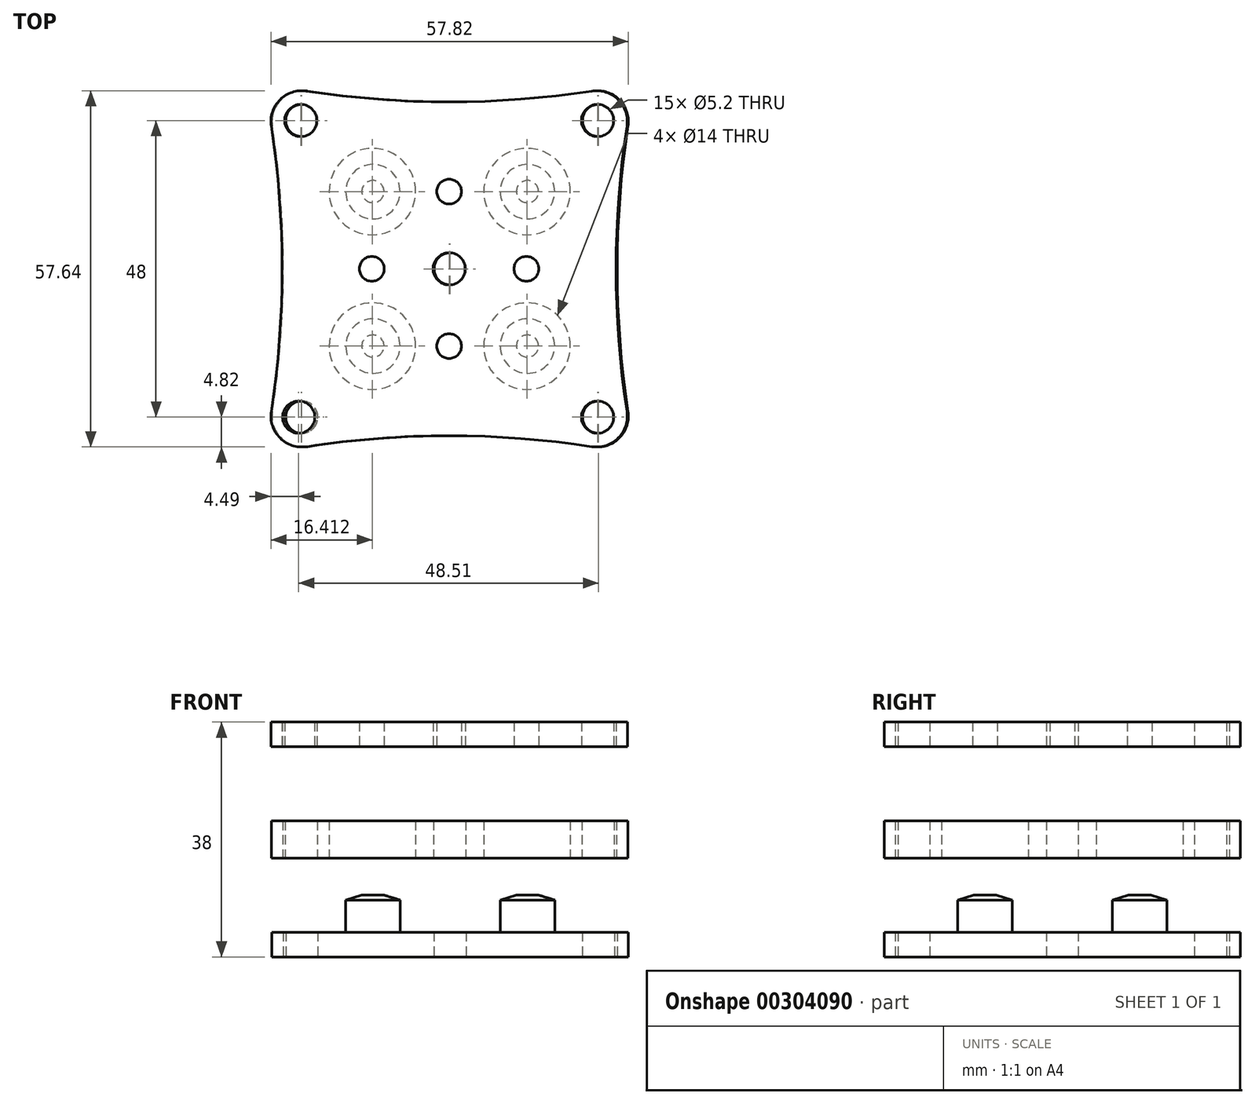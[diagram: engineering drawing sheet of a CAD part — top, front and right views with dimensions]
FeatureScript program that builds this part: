
annotation { "Feature Type Name" : "Feature", "Feature Type Description" : "" }
export const myFeature = defineFeature(function(context is Context, id is Id, definition is map)
    precondition{}
    {
        {
            var Q0;
            Q0=qCreatedBy(makeId("Top.planeOp"),FACE);
            var sketch = newSketch(context, id + "F0", { "sketchPlane" : qUnion([Q0])});
            skLineSegment(sketch, "E0.bottom", {"start": v(12.5, -12.5) * mm, "end": v(-12.5, -12.5) * mm});
            skLineSegment(sketch, "E0.top", {"start": v(12.5, 12.5) * mm, "end": v(-12.5, 12.5) * mm});
            skLineSegment(sketch, "E0.left", {"start": v(12.5, -12.5) * mm, "end": v(12.5, 12.5) * mm});
            skLineSegment(sketch, "E0.right", {"start": v(-12.5, -12.5) * mm, "end": v(-12.5, 12.5) * mm});
            skPoint(sketch, "E0.middle", {"position": v(0, 0) * mm});
            skCircle(sketch, "E1", {"center": v(-12.5, 12.5) * mm, "radius": 7 * mm});
            skCircle(sketch, "E2", {"center": v(12.5, 12.5) * mm, "radius": 7 * mm});
            skCircle(sketch, "E3", {"center": v(-12.5, -12.5) * mm, "radius": 7 * mm});
            skCircle(sketch, "E4", {"center": v(12.5, -12.5) * mm, "radius": 7 * mm});
            skCircle(sketch, "E5", {"center": v(-12.5, 12.5) * mm, "radius": 4.4 * mm});
            skCircle(sketch, "E6", {"center": v(12.5, 12.5) * mm, "radius": 4.4 * mm});
            skCircle(sketch, "E7", {"center": v(12.5, -12.5) * mm, "radius": 4.4 * mm});
            skCircle(sketch, "E8", {"center": v(-12.5, -12.5) * mm, "radius": 4.4 * mm});
            skCircle(sketch, "E9", {"center": v(0, 0) * mm, "radius": 2.6 * mm});
            skLineSegment(sketch, "E10.bottom", {"start": v(30, -30) * mm, "end": v(-30, -30) * mm});
            skLineSegment(sketch, "E10.top", {"start": v(30, 30) * mm, "end": v(-30, 30) * mm});
            skLineSegment(sketch, "E10.left", {"start": v(30, -30) * mm, "end": v(30, 30) * mm});
            skLineSegment(sketch, "E10.right", {"start": v(-30, -30) * mm, "end": v(-30, 30) * mm});
            skPoint(sketch, "E11.centerSnap0", {"position": v(0, -30) * mm});
            skCircle(sketch, "E12.cCircle", {"center": v(0, 0) * mm, "radius": 24 * mm, "construction": true});
            skLineSegment(sketch, "E12.0", {"start": v(24, 24) * mm, "end": v(24, -24) * mm});
            skLineSegment(sketch, "E12.1", {"start": v(24, -24) * mm, "end": v(-24, -24) * mm});
            skLineSegment(sketch, "E12.2", {"start": v(-24, -24) * mm, "end": v(-24, 24) * mm});
            skLineSegment(sketch, "E12.3", {"start": v(-24, 24) * mm, "end": v(24, 24) * mm});
            skPoint(sketch, "E12.0.midPoint", {"position": v(24, 0) * mm});
            skCircle(sketch, "E13", {"center": v(24, 24) * mm, "radius": 2.6 * mm});
            skCircle(sketch, "E14", {"center": v(-24, -24) * mm, "radius": 2.6 * mm});
            skCircle(sketch, "E15", {"center": v(24, -24) * mm, "radius": 2.6 * mm});
            skCircle(sketch, "E16", {"center": v(-24, 24) * mm, "radius": 2.6 * mm});
            skArc(sketch, "E17", {"start": v(-30, 30) * mm, "mid": v(0, 27) * mm, "end": v(30, 30) * mm});
            skArc(sketch, "E18", {"start": v(30, 30) * mm, "mid": v(27, 0) * mm, "end": v(30, -30) * mm});
            skArc(sketch, "E19", {"start": v(30, -30) * mm, "mid": v(0, -27) * mm, "end": v(-30, -30) * mm});
            skArc(sketch, "E20", {"start": v(-30, -30) * mm, "mid": v(-27, 0) * mm, "end": v(-30, 30) * mm});
            skSolve(sketch);
        }
        {
            var Q0;
            Q0=makeQuery(id+"F0.imprint","IMPRINT",FACE,{"disambiguationData":[TD([[makeQuery(id+"F0.imprint","IMPRINT",EDGE,{"derivedFrom":sQuery(id+"F0.wireOp",EDGE,"E17")}),-1.0]])]});
            var Q1;
            {var subQ5=sQuery(id+"F0.wireOp",EDGE,"E4");var subQ6=sQuery(id+"F0.wireOp",EDGE,"E0.bottom");var subQ7=makeQuery(id+"F0.imprint","INTERSECT",VERTEX,{"derivedFrom":[subQ6,subQ5]});Q1=makeQuery(id+"F0.imprint","IMPRINT",FACE,{"disambiguationData":[TD([[makeQuery(id+"F0.imprint","IMPRINT",EDGE,{"disambiguationData":[TD([[subQ7,-1.0]])],"derivedFrom":subQ6}),1.0]])]});}
            var Q2;
            {var subQ0=sQuery(id+"F0.wireOp",EDGE,"E6");var subQ1=sQuery(id+"F0.wireOp",EDGE,"E0.top");var subQ2=makeQuery(id+"F0.imprint","INTERSECT",VERTEX,{"derivedFrom":[subQ1,subQ0]});Q2=makeQuery(id+"F0.imprint","IMPRINT",FACE,{"disambiguationData":[TD([[makeQuery(id+"F0.imprint","IMPRINT",EDGE,{"disambiguationData":[TD([[subQ2,-1.0]])],"derivedFrom":subQ1}),-1.0]])]});}
            var Q3;
            {var subQ0=sQuery(id+"F0.wireOp",EDGE,"E7");var subQ1=sQuery(id+"F0.wireOp",EDGE,"E0.bottom");var subQ2=makeQuery(id+"F0.imprint","INTERSECT",VERTEX,{"derivedFrom":[subQ1,subQ0]});Q3=makeQuery(id+"F0.imprint","IMPRINT",FACE,{"disambiguationData":[TD([[makeQuery(id+"F0.imprint","IMPRINT",EDGE,{"disambiguationData":[TD([[subQ2,-1.0]])],"derivedFrom":subQ1}),1.0]])]});}
            var Q4;
            {var subQ0=sQuery(id+"F0.wireOp",EDGE,"E3");var subQ1=sQuery(id+"F0.wireOp",EDGE,"E0.bottom");var subQ2=makeQuery(id+"F0.imprint","INTERSECT",VERTEX,{"derivedFrom":[subQ1,subQ0]});Q4=makeQuery(id+"F0.imprint","IMPRINT",FACE,{"disambiguationData":[TD([[makeQuery(id+"F0.imprint","IMPRINT",EDGE,{"disambiguationData":[TD([[subQ2,-1.0]])],"derivedFrom":subQ1}),1.0]])]});}
            var Q5;
            {var subQ0=sQuery(id+"F0.wireOp",EDGE,"E1");var subQ1=sQuery(id+"F0.wireOp",EDGE,"E0.top");var subQ2=makeQuery(id+"F0.imprint","INTERSECT",VERTEX,{"derivedFrom":[subQ1,subQ0]});Q5=makeQuery(id+"F0.imprint","IMPRINT",FACE,{"disambiguationData":[TD([[makeQuery(id+"F0.imprint","IMPRINT",EDGE,{"disambiguationData":[TD([[subQ2,-1.0]])],"derivedFrom":subQ1}),-1.0]])]});}
            var Q6;
            Q6=makeQuery(id+"F0.imprint","IMPRINT",FACE,{"disambiguationData":[TD([[makeQuery(id+"F0.imprint","IMPRINT",EDGE,{"derivedFrom":sQuery(id+"F0.wireOp",EDGE,"E9")}),-1.0]])]});
            var Q7;
            {var subQ0=sQuery(id+"F0.wireOp",EDGE,"E7");var subQ1=sQuery(id+"F0.wireOp",EDGE,"E0.bottom");var subQ2=makeQuery(id+"F0.imprint","INTERSECT",VERTEX,{"derivedFrom":[subQ1,subQ0]});Q7=makeQuery(id+"F0.imprint","IMPRINT",FACE,{"disambiguationData":[TD([[makeQuery(id+"F0.imprint","IMPRINT",EDGE,{"disambiguationData":[TD([[subQ2,-1.0]])],"derivedFrom":subQ1}),-1.0]])]});}
            var Q8;
            {var subQ0=sQuery(id+"F0.wireOp",EDGE,"E3");var subQ1=sQuery(id+"F0.wireOp",EDGE,"E0.bottom");var subQ2=makeQuery(id+"F0.imprint","INTERSECT",VERTEX,{"derivedFrom":[subQ1,subQ0]});Q8=makeQuery(id+"F0.imprint","IMPRINT",FACE,{"disambiguationData":[TD([[makeQuery(id+"F0.imprint","IMPRINT",EDGE,{"disambiguationData":[TD([[subQ2,-1.0]])],"derivedFrom":subQ1}),-1.0]])]});}
            var Q9;
            {var subQ0=sQuery(id+"F0.wireOp",EDGE,"E6");var subQ1=sQuery(id+"F0.wireOp",EDGE,"E0.top");var subQ2=makeQuery(id+"F0.imprint","INTERSECT",VERTEX,{"derivedFrom":[subQ1,subQ0]});Q9=makeQuery(id+"F0.imprint","IMPRINT",FACE,{"disambiguationData":[TD([[makeQuery(id+"F0.imprint","IMPRINT",EDGE,{"disambiguationData":[TD([[subQ2,-1.0]])],"derivedFrom":subQ1}),1.0]])]});}
            var Q10;
            {var subQ0=sQuery(id+"F0.wireOp",EDGE,"E1");var subQ1=sQuery(id+"F0.wireOp",EDGE,"E0.top");var subQ2=makeQuery(id+"F0.imprint","INTERSECT",VERTEX,{"derivedFrom":[subQ1,subQ0]});Q10=makeQuery(id+"F0.imprint","IMPRINT",FACE,{"disambiguationData":[TD([[makeQuery(id+"F0.imprint","IMPRINT",EDGE,{"disambiguationData":[TD([[subQ2,-1.0]])],"derivedFrom":subQ1}),1.0]])]});}
            extrude(context, id + "F1", {"entities" : qUnion([Q0, Q1, Q2, Q3, Q4, Q5, Q6, Q7, Q8, Q9, Q10]), "depth" : 4 * mm});
        }
        {
            var Q0;
            {var subQ0=sQuery(id+"F0.wireOp",EDGE,"E0.right");var subQ1=sQuery(id+"F0.wireOp",EDGE,"E0.top");var subQ2=makeQuery(id+"F0.imprint","INTERSECT",VERTEX,{"derivedFrom":[subQ1,subQ0]});Q0=makeQuery(id+"F0.imprint","IMPRINT",FACE,{"disambiguationData":[TD([[makeQuery(id+"F0.imprint","IMPRINT",EDGE,{"disambiguationData":[TD([[subQ2,1.0]])],"derivedFrom":subQ1}),1.0]])]});}
            var Q1;
            {var subQ0=sQuery(id+"F0.wireOp",EDGE,"E0.right");var subQ1=sQuery(id+"F0.wireOp",EDGE,"E0.top");var subQ2=makeQuery(id+"F0.imprint","INTERSECT",VERTEX,{"derivedFrom":[subQ1,subQ0]});Q1=makeQuery(id+"F0.imprint","IMPRINT",FACE,{"disambiguationData":[TD([[makeQuery(id+"F0.imprint","IMPRINT",EDGE,{"disambiguationData":[TD([[subQ2,1.0]])],"derivedFrom":subQ1}),-1.0]])]});}
            var Q2;
            {var subQ0=sQuery(id+"F0.wireOp",EDGE,"E0.left");var subQ1=sQuery(id+"F0.wireOp",EDGE,"E0.top");var subQ2=makeQuery(id+"F0.imprint","INTERSECT",VERTEX,{"derivedFrom":[subQ1,subQ0]});Q2=makeQuery(id+"F0.imprint","IMPRINT",FACE,{"disambiguationData":[TD([[makeQuery(id+"F0.imprint","IMPRINT",EDGE,{"disambiguationData":[TD([[subQ2,-1.0]])],"derivedFrom":subQ1}),1.0]])]});}
            var Q3;
            {var subQ0=sQuery(id+"F0.wireOp",EDGE,"E0.left");var subQ1=sQuery(id+"F0.wireOp",EDGE,"E0.top");var subQ2=makeQuery(id+"F0.imprint","INTERSECT",VERTEX,{"derivedFrom":[subQ1,subQ0]});Q3=makeQuery(id+"F0.imprint","IMPRINT",FACE,{"disambiguationData":[TD([[makeQuery(id+"F0.imprint","IMPRINT",EDGE,{"disambiguationData":[TD([[subQ2,-1.0]])],"derivedFrom":subQ1}),-1.0]])]});}
            var Q4;
            {var subQ0=sQuery(id+"F0.wireOp",EDGE,"E0.left");var subQ1=sQuery(id+"F0.wireOp",EDGE,"E0.bottom");var subQ2=makeQuery(id+"F0.imprint","INTERSECT",VERTEX,{"derivedFrom":[subQ1,subQ0]});Q4=makeQuery(id+"F0.imprint","IMPRINT",FACE,{"disambiguationData":[TD([[makeQuery(id+"F0.imprint","IMPRINT",EDGE,{"disambiguationData":[TD([[subQ2,-1.0]])],"derivedFrom":subQ1}),1.0]])]});}
            var Q5;
            {var subQ0=sQuery(id+"F0.wireOp",EDGE,"E0.left");var subQ1=sQuery(id+"F0.wireOp",EDGE,"E0.bottom");var subQ2=makeQuery(id+"F0.imprint","INTERSECT",VERTEX,{"derivedFrom":[subQ1,subQ0]});Q5=makeQuery(id+"F0.imprint","IMPRINT",FACE,{"disambiguationData":[TD([[makeQuery(id+"F0.imprint","IMPRINT",EDGE,{"disambiguationData":[TD([[subQ2,-1.0]])],"derivedFrom":subQ1}),-1.0]])]});}
            var Q6;
            {var subQ0=sQuery(id+"F0.wireOp",EDGE,"E0.right");var subQ1=sQuery(id+"F0.wireOp",EDGE,"E0.bottom");var subQ2=makeQuery(id+"F0.imprint","INTERSECT",VERTEX,{"derivedFrom":[subQ1,subQ0]});Q6=makeQuery(id+"F0.imprint","IMPRINT",FACE,{"disambiguationData":[TD([[makeQuery(id+"F0.imprint","IMPRINT",EDGE,{"disambiguationData":[TD([[subQ2,1.0]])],"derivedFrom":subQ1}),-1.0]])]});}
            var Q7;
            {var subQ0=sQuery(id+"F0.wireOp",EDGE,"E0.right");var subQ1=sQuery(id+"F0.wireOp",EDGE,"E0.bottom");var subQ2=makeQuery(id+"F0.imprint","INTERSECT",VERTEX,{"derivedFrom":[subQ1,subQ0]});Q7=makeQuery(id+"F0.imprint","IMPRINT",FACE,{"disambiguationData":[TD([[makeQuery(id+"F0.imprint","IMPRINT",EDGE,{"disambiguationData":[TD([[subQ2,1.0]])],"derivedFrom":subQ1}),1.0]])]});}
            extrude(context, id + "F2", {"entities" : qUnion([Q0, Q1, Q2, Q3, Q4, Q5, Q6, Q7]), "operationType" : NewBodyOperationType.ADD, "depth" : 10 * mm});
        }
        {
            var Q0;
            Q0=qCreatedBy(makeId("Top.planeOp"),FACE);
            var sketch = newSketch(context, id + "F3", { "sketchPlane" : qUnion([Q0])});
            skLineSegment(sketch, "E21.bottom", {"start": v(81.22, -12.5) * mm, "end": v(56.22, -12.5) * mm});
            skLineSegment(sketch, "E21.top", {"start": v(81.22, 12.5) * mm, "end": v(56.22, 12.5) * mm});
            skLineSegment(sketch, "E21.left", {"start": v(81.22, -12.5) * mm, "end": v(81.22, 12.5) * mm});
            skLineSegment(sketch, "E21.right", {"start": v(56.22, -12.5) * mm, "end": v(56.22, 12.5) * mm});
            skPoint(sketch, "E21.middle", {"position": v(68.72, 0) * mm});
            skCircle(sketch, "E22", {"center": v(56.22, 12.5) * mm, "radius": 7 * mm});
            skCircle(sketch, "E23", {"center": v(81.22, 12.5) * mm, "radius": 7 * mm});
            skCircle(sketch, "E24", {"center": v(56.22, -12.5) * mm, "radius": 7 * mm});
            skCircle(sketch, "E25", {"center": v(81.22, -12.5) * mm, "radius": 7 * mm});
            skCircle(sketch, "E26", {"center": v(56.22, 12.5) * mm, "radius": 4.55 * mm});
            skCircle(sketch, "E27", {"center": v(81.22, 12.5) * mm, "radius": 4.55 * mm});
            skCircle(sketch, "E28", {"center": v(81.22, -12.5) * mm, "radius": 4.55 * mm});
            skCircle(sketch, "E29", {"center": v(56.22, -12.5) * mm, "radius": 4.55 * mm});
            skCircle(sketch, "E30", {"center": v(68.72, 0) * mm, "radius": 2.6 * mm});
            skLineSegment(sketch, "E31.bottom", {"start": v(98.72, -30) * mm, "end": v(38.72, -30) * mm});
            skLineSegment(sketch, "E31.top", {"start": v(98.72, 30) * mm, "end": v(38.72, 30) * mm});
            skLineSegment(sketch, "E31.left", {"start": v(98.72, -30) * mm, "end": v(98.72, 30) * mm});
            skLineSegment(sketch, "E31.right", {"start": v(38.72, -30) * mm, "end": v(38.72, 30) * mm});
            skPoint(sketch, "E32.centerSnap0", {"position": v(68.72, -30) * mm});
            skCircle(sketch, "E33.cCircle", {"center": v(68.72, 0) * mm, "radius": 24 * mm, "construction": true});
            skLineSegment(sketch, "E33.0", {"start": v(92.72, 24) * mm, "end": v(92.72, -24) * mm});
            skLineSegment(sketch, "E33.1", {"start": v(92.72, -24) * mm, "end": v(44.39, -24) * mm});
            skLineSegment(sketch, "E33.3", {"start": v(44.72, 24) * mm, "end": v(92.72, 24) * mm});
            skPoint(sketch, "E33.0.midPoint", {"position": v(92.72, 0) * mm});
            skCircle(sketch, "E34", {"center": v(92.72, 24) * mm, "radius": 2.6 * mm});
            skCircle(sketch, "E35", {"center": v(44.39, -24) * mm, "radius": 2.6 * mm});
            skCircle(sketch, "E36", {"center": v(92.72, -24) * mm, "radius": 2.6 * mm});
            skCircle(sketch, "E37", {"center": v(44.72, 24) * mm, "radius": 2.6 * mm});
            skArc(sketch, "E38", {"start": v(38.72, 30) * mm, "mid": v(68.72, 27) * mm, "end": v(98.72, 30) * mm});
            skArc(sketch, "E39", {"start": v(98.72, 30) * mm, "mid": v(95.72, 0) * mm, "end": v(98.72, -30) * mm});
            skArc(sketch, "E40", {"start": v(98.72, -30) * mm, "mid": v(68.72, -27) * mm, "end": v(38.72, -30) * mm});
            skArc(sketch, "E41", {"start": v(38.72, -30) * mm, "mid": v(41.72, 0) * mm, "end": v(38.72, 30) * mm});
            skCircle(sketch, "E42", {"center": v(68.72, 12.5) * mm, "radius": 2 * mm});
            skCircle(sketch, "E43", {"center": v(56.22, 0) * mm, "radius": 2 * mm});
            skCircle(sketch, "E44", {"center": v(68.72, -12.5) * mm, "radius": 2 * mm});
            skCircle(sketch, "E45", {"center": v(81.22, 0) * mm, "radius": 2 * mm});
            skSolve(sketch);
        }
        {
            var Q0;
            Q0=makeQuery(id+"F3.imprint","IMPRINT",FACE,{"disambiguationData":[TD([[makeQuery(id+"F3.imprint","IMPRINT",EDGE,{"derivedFrom":sQuery(id+"F3.wireOp",EDGE,"E35")}),-1.0]])]});
            var Q1;
            Q1=makeQuery(id+"F3.imprint","IMPRINT",FACE,{"disambiguationData":[TD([[makeQuery(id+"F3.imprint","IMPRINT",EDGE,{"derivedFrom":sQuery(id+"F3.wireOp",EDGE,"E30")}),-1.0]])]});
            var Q2;
            {var subQ0=sQuery(id+"F3.wireOp",EDGE,"E22");var subQ1=sQuery(id+"F3.wireOp",EDGE,"E21.top");var subQ2=makeQuery(id+"F3.imprint","INTERSECT",VERTEX,{"derivedFrom":[subQ1,subQ0]});Q2=makeQuery(id+"F3.imprint","IMPRINT",FACE,{"disambiguationData":[TD([[makeQuery(id+"F3.imprint","IMPRINT",EDGE,{"disambiguationData":[TD([[subQ2,-1.0]])],"derivedFrom":subQ1}),-1.0]])]});}
            var Q3;
            {var subQ0=sQuery(id+"F3.wireOp",EDGE,"E22");var subQ1=sQuery(id+"F3.wireOp",EDGE,"E21.top");var subQ2=makeQuery(id+"F3.imprint","INTERSECT",VERTEX,{"derivedFrom":[subQ1,subQ0]});Q3=makeQuery(id+"F3.imprint","IMPRINT",FACE,{"disambiguationData":[TD([[makeQuery(id+"F3.imprint","IMPRINT",EDGE,{"disambiguationData":[TD([[subQ2,-1.0]])],"derivedFrom":subQ1}),1.0]])]});}
            var Q4;
            {var subQ0=sQuery(id+"F3.wireOp",EDGE,"E24");var subQ1=sQuery(id+"F3.wireOp",EDGE,"E21.bottom");var subQ2=makeQuery(id+"F3.imprint","INTERSECT",VERTEX,{"derivedFrom":[subQ1,subQ0]});Q4=makeQuery(id+"F3.imprint","IMPRINT",FACE,{"disambiguationData":[TD([[makeQuery(id+"F3.imprint","IMPRINT",EDGE,{"disambiguationData":[TD([[subQ2,-1.0]])],"derivedFrom":subQ1}),1.0]])]});}
            var Q5;
            {var subQ0=sQuery(id+"F3.wireOp",EDGE,"E24");var subQ1=sQuery(id+"F3.wireOp",EDGE,"E21.bottom");var subQ2=makeQuery(id+"F3.imprint","INTERSECT",VERTEX,{"derivedFrom":[subQ1,subQ0]});Q5=makeQuery(id+"F3.imprint","IMPRINT",FACE,{"disambiguationData":[TD([[makeQuery(id+"F3.imprint","IMPRINT",EDGE,{"disambiguationData":[TD([[subQ2,-1.0]])],"derivedFrom":subQ1}),-1.0]])]});}
            var Q6;
            {var subQ0=sQuery(id+"F3.wireOp",EDGE,"E27");var subQ1=sQuery(id+"F3.wireOp",EDGE,"E21.top");var subQ2=makeQuery(id+"F3.imprint","INTERSECT",VERTEX,{"derivedFrom":[subQ1,subQ0]});Q6=makeQuery(id+"F3.imprint","IMPRINT",FACE,{"disambiguationData":[TD([[makeQuery(id+"F3.imprint","IMPRINT",EDGE,{"disambiguationData":[TD([[subQ2,-1.0]])],"derivedFrom":subQ1}),1.0]])]});}
            var Q7;
            {var subQ0=sQuery(id+"F3.wireOp",EDGE,"E27");var subQ1=sQuery(id+"F3.wireOp",EDGE,"E21.top");var subQ2=makeQuery(id+"F3.imprint","INTERSECT",VERTEX,{"derivedFrom":[subQ1,subQ0]});Q7=makeQuery(id+"F3.imprint","IMPRINT",FACE,{"disambiguationData":[TD([[makeQuery(id+"F3.imprint","IMPRINT",EDGE,{"disambiguationData":[TD([[subQ2,-1.0]])],"derivedFrom":subQ1}),-1.0]])]});}
            var Q8;
            {var subQ0=sQuery(id+"F3.wireOp",EDGE,"E28");var subQ1=sQuery(id+"F3.wireOp",EDGE,"E21.bottom");var subQ2=makeQuery(id+"F3.imprint","INTERSECT",VERTEX,{"derivedFrom":[subQ1,subQ0]});Q8=makeQuery(id+"F3.imprint","IMPRINT",FACE,{"disambiguationData":[TD([[makeQuery(id+"F3.imprint","IMPRINT",EDGE,{"disambiguationData":[TD([[subQ2,-1.0]])],"derivedFrom":subQ1}),1.0]])]});}
            var Q9;
            {var subQ0=sQuery(id+"F3.wireOp",EDGE,"E28");var subQ1=sQuery(id+"F3.wireOp",EDGE,"E21.bottom");var subQ2=makeQuery(id+"F3.imprint","INTERSECT",VERTEX,{"derivedFrom":[subQ1,subQ0]});Q9=makeQuery(id+"F3.imprint","IMPRINT",FACE,{"disambiguationData":[TD([[makeQuery(id+"F3.imprint","IMPRINT",EDGE,{"disambiguationData":[TD([[subQ2,-1.0]])],"derivedFrom":subQ1}),-1.0]])]});}
            var Q10;
            {var subQ0=sQuery(id+"F3.wireOp",EDGE,"E21.left");var subQ1=sQuery(id+"F3.wireOp",EDGE,"E21.top");var subQ2=makeQuery(id+"F3.imprint","INTERSECT",VERTEX,{"derivedFrom":[subQ1,subQ0]});Q10=makeQuery(id+"F3.imprint","IMPRINT",FACE,{"disambiguationData":[TD([[makeQuery(id+"F3.imprint","IMPRINT",EDGE,{"disambiguationData":[TD([[subQ2,-1.0]])],"derivedFrom":subQ1}),-1.0]])]});}
            var Q11;
            {var subQ0=sQuery(id+"F3.wireOp",EDGE,"E21.left");var subQ1=sQuery(id+"F3.wireOp",EDGE,"E21.top");var subQ2=makeQuery(id+"F3.imprint","INTERSECT",VERTEX,{"derivedFrom":[subQ1,subQ0]});Q11=makeQuery(id+"F3.imprint","IMPRINT",FACE,{"disambiguationData":[TD([[makeQuery(id+"F3.imprint","IMPRINT",EDGE,{"disambiguationData":[TD([[subQ2,-1.0]])],"derivedFrom":subQ1}),1.0]])]});}
            var Q12;
            {var subQ0=sQuery(id+"F3.wireOp",EDGE,"E21.right");var subQ1=sQuery(id+"F3.wireOp",EDGE,"E21.top");var subQ2=makeQuery(id+"F3.imprint","INTERSECT",VERTEX,{"derivedFrom":[subQ1,subQ0]});Q12=makeQuery(id+"F3.imprint","IMPRINT",FACE,{"disambiguationData":[TD([[makeQuery(id+"F3.imprint","IMPRINT",EDGE,{"disambiguationData":[TD([[subQ2,1.0]])],"derivedFrom":subQ1}),-1.0]])]});}
            var Q13;
            {var subQ0=sQuery(id+"F3.wireOp",EDGE,"E21.right");var subQ1=sQuery(id+"F3.wireOp",EDGE,"E21.top");var subQ2=makeQuery(id+"F3.imprint","INTERSECT",VERTEX,{"derivedFrom":[subQ1,subQ0]});Q13=makeQuery(id+"F3.imprint","IMPRINT",FACE,{"disambiguationData":[TD([[makeQuery(id+"F3.imprint","IMPRINT",EDGE,{"disambiguationData":[TD([[subQ2,1.0]])],"derivedFrom":subQ1}),1.0]])]});}
            var Q14;
            {var subQ0=sQuery(id+"F3.wireOp",EDGE,"E21.right");var subQ1=sQuery(id+"F3.wireOp",EDGE,"E21.bottom");var subQ2=makeQuery(id+"F3.imprint","INTERSECT",VERTEX,{"derivedFrom":[subQ1,subQ0]});Q14=makeQuery(id+"F3.imprint","IMPRINT",FACE,{"disambiguationData":[TD([[makeQuery(id+"F3.imprint","IMPRINT",EDGE,{"disambiguationData":[TD([[subQ2,1.0]])],"derivedFrom":subQ1}),-1.0]])]});}
            var Q15;
            {var subQ0=sQuery(id+"F3.wireOp",EDGE,"E21.right");var subQ1=sQuery(id+"F3.wireOp",EDGE,"E21.bottom");var subQ2=makeQuery(id+"F3.imprint","INTERSECT",VERTEX,{"derivedFrom":[subQ1,subQ0]});Q15=makeQuery(id+"F3.imprint","IMPRINT",FACE,{"disambiguationData":[TD([[makeQuery(id+"F3.imprint","IMPRINT",EDGE,{"disambiguationData":[TD([[subQ2,1.0]])],"derivedFrom":subQ1}),1.0]])]});}
            var Q16;
            {var subQ0=sQuery(id+"F3.wireOp",EDGE,"E21.left");var subQ1=sQuery(id+"F3.wireOp",EDGE,"E21.bottom");var subQ2=makeQuery(id+"F3.imprint","INTERSECT",VERTEX,{"derivedFrom":[subQ1,subQ0]});Q16=makeQuery(id+"F3.imprint","IMPRINT",FACE,{"disambiguationData":[TD([[makeQuery(id+"F3.imprint","IMPRINT",EDGE,{"disambiguationData":[TD([[subQ2,-1.0]])],"derivedFrom":subQ1}),1.0]])]});}
            var Q17;
            {var subQ0=sQuery(id+"F3.wireOp",EDGE,"E21.left");var subQ1=sQuery(id+"F3.wireOp",EDGE,"E21.bottom");var subQ2=makeQuery(id+"F3.imprint","INTERSECT",VERTEX,{"derivedFrom":[subQ1,subQ0]});Q17=makeQuery(id+"F3.imprint","IMPRINT",FACE,{"disambiguationData":[TD([[makeQuery(id+"F3.imprint","IMPRINT",EDGE,{"disambiguationData":[TD([[subQ2,-1.0]])],"derivedFrom":subQ1}),-1.0]])]});}
            extrude(context, id + "F4", {"entities" : qUnion([Q0, Q1, Q2, Q3, Q4, Q5, Q6, Q7, Q8, Q9, Q10, Q11, Q12, Q13, Q14, Q15, Q16, Q17]), "depth" : 4 * mm});
        }
        {
            var Q0;
            Q0=qCreatedBy(makeId("Top.planeOp"),FACE);
            var sketch = newSketch(context, id + "F5", { "sketchPlane" : qUnion([Q0])});
            skLineSegment(sketch, "E46.bottom", {"start": v(-70.39, -12.5) * mm, "end": v(-95.39, -12.5) * mm});
            skLineSegment(sketch, "E46.top", {"start": v(-70.39, 12.5) * mm, "end": v(-95.39, 12.5) * mm});
            skLineSegment(sketch, "E46.left", {"start": v(-70.39, -12.5) * mm, "end": v(-70.39, 12.5) * mm});
            skLineSegment(sketch, "E46.right", {"start": v(-95.39, -12.5) * mm, "end": v(-95.39, 12.5) * mm});
            skPoint(sketch, "E46.middle", {"position": v(-82.89, 0) * mm});
            skCircle(sketch, "E47", {"center": v(-95.39, 12.5) * mm, "radius": 7 * mm});
            skCircle(sketch, "E48", {"center": v(-70.39, 12.5) * mm, "radius": 7 * mm});
            skCircle(sketch, "E49", {"center": v(-95.39, -12.5) * mm, "radius": 7 * mm});
            skCircle(sketch, "E50", {"center": v(-70.39, -12.5) * mm, "radius": 7 * mm});
            skCircle(sketch, "E51", {"center": v(-95.39, 12.5) * mm, "radius": 4.5 * mm});
            skCircle(sketch, "E52", {"center": v(-70.39, 12.5) * mm, "radius": 4.5 * mm});
            skCircle(sketch, "E53", {"center": v(-70.39, -12.5) * mm, "radius": 4.5 * mm});
            skCircle(sketch, "E54", {"center": v(-95.39, -12.5) * mm, "radius": 4.5 * mm});
            skCircle(sketch, "E55", {"center": v(-82.89, 0) * mm, "radius": 2.6 * mm});
            skLineSegment(sketch, "E56.bottom", {"start": v(-52.89, -30) * mm, "end": v(-112.89, -30) * mm});
            skLineSegment(sketch, "E56.top", {"start": v(-52.89, 30) * mm, "end": v(-112.89, 30) * mm});
            skLineSegment(sketch, "E56.left", {"start": v(-52.89, -30) * mm, "end": v(-52.89, 30) * mm});
            skLineSegment(sketch, "E56.right", {"start": v(-112.89, -30) * mm, "end": v(-112.89, 30) * mm});
            skPoint(sketch, "E57.centerSnap0", {"position": v(-82.89, -30) * mm});
            skCircle(sketch, "E58.cCircle", {"center": v(-82.89, 0) * mm, "radius": 24 * mm, "construction": true});
            skLineSegment(sketch, "E58.0", {"start": v(-58.89, 24) * mm, "end": v(-58.89, -24) * mm});
            skLineSegment(sketch, "E58.1", {"start": v(-58.89, -24) * mm, "end": v(-106.89, -24) * mm});
            skLineSegment(sketch, "E58.3", {"start": v(-106.89, 24) * mm, "end": v(-58.89, 24) * mm});
            skPoint(sketch, "E58.0.midPoint", {"position": v(-58.89, 0) * mm});
            skCircle(sketch, "E59", {"center": v(-58.89, 24) * mm, "radius": 2.6 * mm});
            skCircle(sketch, "E60", {"center": v(-106.89, -24) * mm, "radius": 2.6 * mm});
            skCircle(sketch, "E61", {"center": v(-58.89, -24) * mm, "radius": 2.6 * mm});
            skCircle(sketch, "E62", {"center": v(-106.89, 24) * mm, "radius": 2.6 * mm});
            skArc(sketch, "E63", {"start": v(-112.89, 30) * mm, "mid": v(-82.89, 27) * mm, "end": v(-52.89, 30) * mm});
            skArc(sketch, "E64", {"start": v(-52.89, 30) * mm, "mid": v(-55.89, 0) * mm, "end": v(-52.89, -30) * mm});
            skArc(sketch, "E65", {"start": v(-52.89, -30) * mm, "mid": v(-82.89, -27) * mm, "end": v(-112.89, -30) * mm});
            skArc(sketch, "E66", {"start": v(-112.89, -30) * mm, "mid": v(-109.89, 0) * mm, "end": v(-112.89, 30) * mm});
            skSolve(sketch);
        }
        {
            var Q0;
            Q0=makeQuery(id+"F5.imprint","IMPRINT",FACE,{"disambiguationData":[TD([[makeQuery(id+"F5.imprint","IMPRINT",EDGE,{"derivedFrom":sQuery(id+"F5.wireOp",EDGE,"E60")}),-1.0]])]});
            var Q1;
            Q1=makeQuery(id+"F5.imprint","IMPRINT",FACE,{"disambiguationData":[TD([[makeQuery(id+"F5.imprint","IMPRINT",EDGE,{"derivedFrom":sQuery(id+"F5.wireOp",EDGE,"E55")}),-1.0]])]});
            extrude(context, id + "F6", {"entities" : qUnion([Q0, Q1]), "depth" : 6 * mm});
        }
        {
            var Q0;
            Q0=makeQuery(id+"F1.opExtrude","SWEPT_EDGE",EDGE,{"disambiguationData":[OSD([sQuery(id+"F0.wireOp",EDGE,"E10.bottom"),sQuery(id+"F0.wireOp",EDGE,"E10.left"),sQuery(id+"F0.wireOp",EDGE,"E18"),sQuery(id+"F0.wireOp",EDGE,"E19")])]});
            var Q1;
            Q1=makeQuery(id+"F1.opExtrude","SWEPT_EDGE",EDGE,{"disambiguationData":[OSD([sQuery(id+"F0.wireOp",EDGE,"E10.bottom"),sQuery(id+"F0.wireOp",EDGE,"E10.right"),sQuery(id+"F0.wireOp",EDGE,"E19"),sQuery(id+"F0.wireOp",EDGE,"E20")])]});
            var Q2;
            Q2=makeQuery(id+"F1.opExtrude","SWEPT_EDGE",EDGE,{"disambiguationData":[OSD([sQuery(id+"F0.wireOp",EDGE,"E10.top"),sQuery(id+"F0.wireOp",EDGE,"E10.left"),sQuery(id+"F0.wireOp",EDGE,"E17"),sQuery(id+"F0.wireOp",EDGE,"E18")])]});
            var Q3;
            Q3=makeQuery(id+"F1.opExtrude","SWEPT_EDGE",EDGE,{"disambiguationData":[OSD([sQuery(id+"F0.wireOp",EDGE,"E10.top"),sQuery(id+"F0.wireOp",EDGE,"E10.right"),sQuery(id+"F0.wireOp",EDGE,"E17"),sQuery(id+"F0.wireOp",EDGE,"E20")])]});
            var Q4;
            Q4=makeQuery(id+"F4.opExtrude","SWEPT_EDGE",EDGE,{"disambiguationData":[OSD([sQuery(id+"F3.wireOp",EDGE,"E31.bottom"),sQuery(id+"F3.wireOp",EDGE,"E31.right"),sQuery(id+"F3.wireOp",EDGE,"E40"),sQuery(id+"F3.wireOp",EDGE,"E41")])]});
            var Q5;
            Q5=makeQuery(id+"F4.opExtrude","SWEPT_EDGE",EDGE,{"disambiguationData":[OSD([sQuery(id+"F3.wireOp",EDGE,"E31.bottom"),sQuery(id+"F3.wireOp",EDGE,"E31.left"),sQuery(id+"F3.wireOp",EDGE,"E39"),sQuery(id+"F3.wireOp",EDGE,"E40")])]});
            var Q6;
            Q6=makeQuery(id+"F4.opExtrude","SWEPT_EDGE",EDGE,{"disambiguationData":[OSD([sQuery(id+"F3.wireOp",EDGE,"E31.top"),sQuery(id+"F3.wireOp",EDGE,"E31.left"),sQuery(id+"F3.wireOp",EDGE,"E38"),sQuery(id+"F3.wireOp",EDGE,"E39")])]});
            var Q7;
            Q7=makeQuery(id+"F4.opExtrude","SWEPT_EDGE",EDGE,{"disambiguationData":[OSD([sQuery(id+"F3.wireOp",EDGE,"E31.top"),sQuery(id+"F3.wireOp",EDGE,"E31.right"),sQuery(id+"F3.wireOp",EDGE,"E38"),sQuery(id+"F3.wireOp",EDGE,"E41")])]});
            fillet(context, id + "F7", {"entities" : qUnion([Q0, Q1, Q2, Q3, Q4, Q5, Q6, Q7]), "radius" : 5 * mm, "tangentPropagation" : true, "allowEdgeOverflow" : false});
        }
        {
            var Q0;
            Q0=makeQuery(id+"F6.opExtrude","SWEPT_EDGE",EDGE,{"disambiguationData":[OSD([sQuery(id+"F5.wireOp",EDGE,"E56.bottom"),sQuery(id+"F5.wireOp",EDGE,"E56.right"),sQuery(id+"F5.wireOp",EDGE,"E65"),sQuery(id+"F5.wireOp",EDGE,"E66")])]});
            var Q1;
            Q1=makeQuery(id+"F6.opExtrude","SWEPT_EDGE",EDGE,{"disambiguationData":[OSD([sQuery(id+"F5.wireOp",EDGE,"E56.bottom"),sQuery(id+"F5.wireOp",EDGE,"E56.left"),sQuery(id+"F5.wireOp",EDGE,"E64"),sQuery(id+"F5.wireOp",EDGE,"E65")])]});
            var Q2;
            Q2=makeQuery(id+"F6.opExtrude","SWEPT_EDGE",EDGE,{"disambiguationData":[OSD([sQuery(id+"F5.wireOp",EDGE,"E56.top"),sQuery(id+"F5.wireOp",EDGE,"E56.left"),sQuery(id+"F5.wireOp",EDGE,"E63"),sQuery(id+"F5.wireOp",EDGE,"E64")])]});
            var Q3;
            Q3=makeQuery(id+"F6.opExtrude","SWEPT_EDGE",EDGE,{"disambiguationData":[OSD([sQuery(id+"F5.wireOp",EDGE,"E56.top"),sQuery(id+"F5.wireOp",EDGE,"E56.right"),sQuery(id+"F5.wireOp",EDGE,"E63"),sQuery(id+"F5.wireOp",EDGE,"E66")])]});
            fillet(context, id + "F8", {"entities" : qUnion([Q0, Q1, Q2, Q3]), "radius" : 5 * mm, "tangentPropagation" : true, "allowEdgeOverflow" : false});
        }
        {
            var Q0;
            Q0=makeQuery(id+"F2.opExtrude","CAP_EDGE",EDGE,{"disambiguationData":[OSD([sQuery(id+"F0.wireOp",EDGE,"E5")])],"isStart":false});
            var Q1;
            Q1=makeQuery(id+"F2.opExtrude","CAP_EDGE",EDGE,{"disambiguationData":[OSD([sQuery(id+"F0.wireOp",EDGE,"E8")])],"isStart":false});
            var Q2;
            Q2=makeQuery(id+"F2.opExtrude","CAP_EDGE",EDGE,{"disambiguationData":[OSD([sQuery(id+"F0.wireOp",EDGE,"E7")])],"isStart":false});
            var Q3;
            Q3=makeQuery(id+"F2.opExtrude","CAP_EDGE",EDGE,{"disambiguationData":[OSD([sQuery(id+"F0.wireOp",EDGE,"E6")])],"isStart":false});
            chamfer(context, id + "F9", {"entities" : qUnion([Q0, Q1, Q2, Q3]), "chamferType" : ChamferType.TWO_OFFSETS, "width1" : 2.6 * mm, "oppositeDirection" : false, "width2" : 0.8 * mm, "tangentPropagation" : true});
        }
        {
            var Q0;
            Q0=makeQuery(id+"F4.opExtrude","SWEPT_BODY",BODY,{"disambiguationData":[OSD([sQuery(id+"F3.wireOp",EDGE,"E30"),sQuery(id+"F3.wireOp",EDGE,"E34"),sQuery(id+"F3.wireOp",EDGE,"E35"),sQuery(id+"F3.wireOp",EDGE,"E36"),sQuery(id+"F3.wireOp",EDGE,"E37"),sQuery(id+"F3.wireOp",EDGE,"E38"),sQuery(id+"F3.wireOp",EDGE,"E39"),sQuery(id+"F3.wireOp",EDGE,"E40"),sQuery(id+"F3.wireOp",EDGE,"E41"),sQuery(id+"F3.wireOp",EDGE,"E42"),sQuery(id+"F3.wireOp",EDGE,"E43"),sQuery(id+"F3.wireOp",EDGE,"E44"),sQuery(id+"F3.wireOp",EDGE,"E45")])]});
            transform(context, id + "F10", {"entities" : qUnion([Q0]), "transformType" : TransformType.TRANSLATION_3D, "dx" : -68.9 * mm, "dy" : 0 * mm, "dz" : 34 * mm, "makeCopy" : false});
        }
        {
            var Q0;
            Q0=makeQuery(id+"F6.opExtrude","SWEPT_BODY",BODY,{"disambiguationData":[OSD([sQuery(id+"F5.wireOp",EDGE,"E47"),sQuery(id+"F5.wireOp",EDGE,"E48"),sQuery(id+"F5.wireOp",EDGE,"E49"),sQuery(id+"F5.wireOp",EDGE,"E50"),sQuery(id+"F5.wireOp",EDGE,"E55"),sQuery(id+"F5.wireOp",EDGE,"E59"),sQuery(id+"F5.wireOp",EDGE,"E60"),sQuery(id+"F5.wireOp",EDGE,"E61"),sQuery(id+"F5.wireOp",EDGE,"E62"),sQuery(id+"F5.wireOp",EDGE,"E63"),sQuery(id+"F5.wireOp",EDGE,"E64"),sQuery(id+"F5.wireOp",EDGE,"E65"),sQuery(id+"F5.wireOp",EDGE,"E66")])]});
            transform(context, id + "F11", {"entities" : qUnion([Q0]), "transformType" : TransformType.TRANSLATION_3D, "dx" : 82.8 * mm, "dy" : 0 * mm, "dz" : 16 * mm, "makeCopy" : false});
        }
    });
